# Revit family: mcr FID-НЗ-К1-ВЗ-D
name_source: partatom
category: Арматура воздуховодов
revit_build: Autodesk Revit 2016 (Build: 20150714_1515(x64)
units: mm (PartAtom-declared; Revit-internal decimal feet)

## family parameters
Всегда вертикально = Да
На основе рабочей плоскости = Нет
Общий = Да
При загрузке вырезать с полостями = Нет
Размер круглого соединителя = Использовать диаметр
Тип детали = Вставляется

## types (2) — shared parameters
BF230 = Нет
BF24 = Нет
BFL230 = Нет
BFL24 = Нет
BFN230 = Нет
BFN24 = Нет
MM230 = Нет
MM24 = Нет
P = 1.2000 кг/куб. м
Клеммная колодка = Нет
Материал клапана = <По категории>
Морозостойкое исполнение = Нет
Оснащение привода саморегулирующимся нагревательным кабелем = Нет
Распаячная коробка с КК = Нет
Термодатчик = Нет
Толщина заслонки = 10 мм
Толщина стенки = 3 мм
ЭМ230 = Нет
ЭМ24 = Нет
zero-valued in all types: ADSK_Масса

## per-type parameters (varying)
| type | ID_EI |
| EI90 | 90 мм |
| EI120 | 120 мм |

note: column(s) folded — value = type name in every type: EI

## geometry (parser evidence)
native form markers: Blend x2
no freeform markers — native parametric forms only
